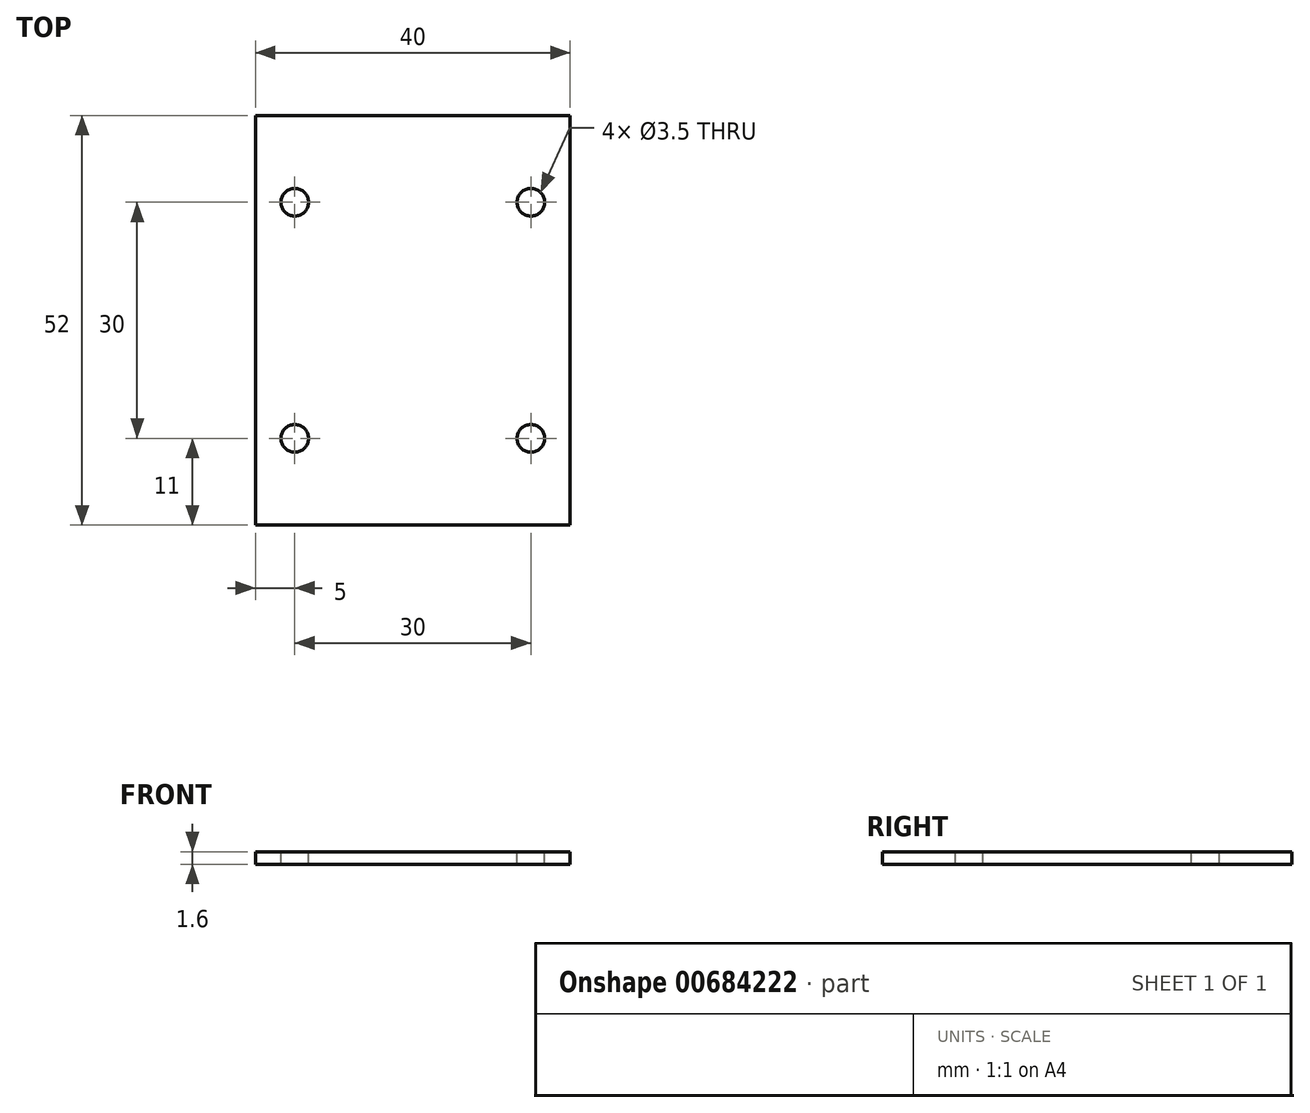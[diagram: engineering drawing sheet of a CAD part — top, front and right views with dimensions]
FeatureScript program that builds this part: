
annotation { "Feature Type Name" : "Feature", "Feature Type Description" : "" }
export const myFeature = defineFeature(function(context is Context, id is Id, definition is map)
    precondition{}
    {
        {
            var Q0;
            Q0=qCreatedBy(makeId("Top.planeOp"),FACE);
            var sketch = newSketch(context, id + "F0", { "sketchPlane" : qUnion([Q0])});
            skLineSegment(sketch, "E0.bottom", {"start": v(20, -26) * mm, "end": v(-20, -26) * mm});
            skLineSegment(sketch, "E0.top", {"start": v(20, 26) * mm, "end": v(-20, 26) * mm});
            skLineSegment(sketch, "E0.left", {"start": v(20, -26) * mm, "end": v(20, 26) * mm});
            skLineSegment(sketch, "E0.right", {"start": v(-20, -26) * mm, "end": v(-20, 26) * mm});
            skPoint(sketch, "E0.middle", {"position": v(0, 0) * mm});
            skSolve(sketch);
        }
        {
            var Q0;
            Q0=makeQuery(id+"F0.imprint","IMPRINT",FACE,{"disambiguationData":[TD([[makeQuery(id+"F0.imprint","IMPRINT",EDGE,{"derivedFrom":sQuery(id+"F0.wireOp",EDGE,"E0.bottom")}),-1.0]])]});
            extrude(context, id + "F1", {"entities" : qUnion([Q0]), "endBound" : BoundingType.SYMMETRIC, "depth" : 1.6 * mm, "offsetDistance" : 25 * mm});
        }
        {
            var Q0;
            Q0=makeQuery(id+"F1.opExtrude","CAP_FACE",FACE,{"disambiguationData":[OSD([sQuery(id+"F0.wireOp",EDGE,"E0.bottom"),sQuery(id+"F0.wireOp",EDGE,"E0.top"),sQuery(id+"F0.wireOp",EDGE,"E0.left"),sQuery(id+"F0.wireOp",EDGE,"E0.right")])],"isStart":false});
            var sketch = newSketch(context, id + "F2", { "sketchPlane" : qUnion([Q0])});
            skLineSegment(sketch, "E1.bottom", {"start": v(15, -15) * mm, "end": v(-15, -15) * mm, "construction": true});
            skLineSegment(sketch, "E1.top", {"start": v(15, 15) * mm, "end": v(-15, 15) * mm, "construction": true});
            skLineSegment(sketch, "E1.left", {"start": v(15, -15) * mm, "end": v(15, 15) * mm, "construction": true});
            skLineSegment(sketch, "E1.right", {"start": v(-15, -15) * mm, "end": v(-15, 15) * mm, "construction": true});
            skPoint(sketch, "E1.middle", {"position": v(0, 0) * mm});
            skCircle(sketch, "E2", {"center": v(-15, 15) * mm, "radius": 1.75 * mm});
            skCircle(sketch, "E3", {"center": v(15, 15) * mm, "radius": 1.75 * mm});
            skCircle(sketch, "E4", {"center": v(-15, -15) * mm, "radius": 1.75 * mm});
            skCircle(sketch, "E5", {"center": v(15, -15) * mm, "radius": 1.75 * mm});
            skSolve(sketch);
        }
        {
            var Q0;
            Q0 = qSketchRegion(id + "F2", true);
            extrude(context, id + "F3", {"entities" : qUnion([Q0]), "operationType" : NewBodyOperationType.REMOVE, "endBound" : BoundingType.UP_TO_NEXT, "oppositeDirection" : true, "depth" : 25 * mm, "offsetDistance" : 25 * mm});
        }
    });
